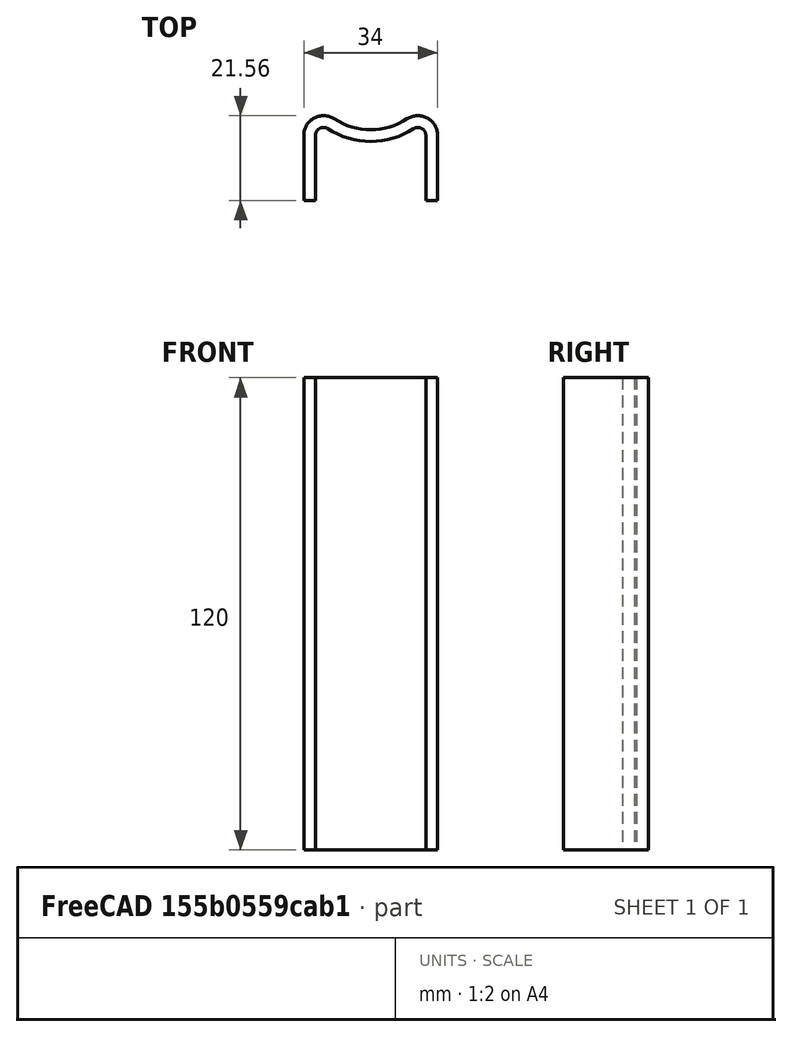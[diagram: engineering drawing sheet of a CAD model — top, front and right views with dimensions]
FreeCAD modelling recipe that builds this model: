
FCSTD DOCUMENT  (FreeCAD 0.18R4 (GitTag))
Label: door-rod-holder
License: All rights reserved
LicenseURL: http://en.wikipedia.org/wiki/All_rights_reserved
objects: Sketcher::SketchObject×1, PartDesign::Pad×1, PartDesign::Body×1
note: 4 computed .brp shape members not serialized (recipe doc carries the construction recipe); baked Part::Feature solids carry a one-line shape summary decoded from their .brp

FEATURE [Sketcher::SketchObject] Sketch
  MapMode = 5
  Support = -> [XY_Plane]
  sketch-geometry (12):
    g0: LineSegment StartX=0 StartY=0 StartZ=0 EndX=3 EndY=0 EndZ=0
    g1: LineSegment StartX=34 StartY=0 StartZ=0 EndX=34 EndY=16.561 EndZ=0
    g2: LineSegment StartX=0 StartY=16.561 StartZ=0 EndX=0 EndY=0 EndZ=0
    g3: LineSegment StartX=31 StartY=16.561 StartZ=0 EndX=31 EndY=0 EndZ=0
    g4: LineSegment StartX=3 StartY=0 StartZ=0 EndX=3 EndY=16.561 EndZ=0
    g5: LineSegment StartX=31 StartY=0 StartZ=0 EndX=34 EndY=0 EndZ=0
    g6: ArcOfCircle CenterX=5 CenterY=16.561 CenterZ=0 NormalX=0 NormalY=0 NormalZ=1 AngleXU=0 Radius=5 StartAngle=0.993864 EndAngle=3.14159
    g7: ArcOfCircle CenterX=17 CenterY=35.0001 CenterZ=0 NormalX=0 NormalY=0 NormalZ=1 AngleXU=0 Radius=17 StartAngle=4.13546 EndAngle=5.28932
    g8: ArcOfCircle CenterX=29 CenterY=16.561 CenterZ=0 NormalX=0 NormalY=0 NormalZ=1 AngleXU=0 Radius=5 StartAngle=6.28319 EndAngle=8.43092
    g9: ArcOfCircle CenterX=29 CenterY=16.561 CenterZ=0 NormalX=0 NormalY=0 NormalZ=1 AngleXU=0 Radius=2 StartAngle=3.71277e-08 EndAngle=2.14773
    g10: ArcOfCircle CenterX=17 CenterY=35.0001 CenterZ=0 NormalX=0 NormalY=0 NormalZ=1 AngleXU=0 Radius=20 StartAngle=4.13546 EndAngle=5.28932
    g11: ArcOfCircle CenterX=5 CenterY=16.561 CenterZ=0 NormalX=0 NormalY=0 NormalZ=1 AngleXU=0 Radius=2 StartAngle=0.993865 EndAngle=3.14159
  constraints (40):
    c: Coincident(g5,g1)
    c: Coincident(g2,g0)
    c: Horizontal(g0)
    c: Vertical(g1)
    c: Vertical(g2)
    c: Coincident(g0,g-1)
    c: Vertical(g3)
    c: Vertical(g4)
    c: Tangent(g0,g5)
    c: Coincident(g4,g0)
    c: Coincident(g3,g5)
    c: Coincident(g6,g2)
    c: Coincident(g7,g6)
    c: Coincident(g8,g7)
    c: Coincident(g8,g1)
    c: Coincident(g9,g3)
    c: Coincident(g10,g9)
    c: Coincident(g11,g10)
    c: Coincident(g11,g4)
    c: DistanceX(g3,g1) = 3
    c: DistanceX(g0,g0) = 3
    c: DistanceX(g0,g1) = 34
    c: Radius(g8) = 5
    c: Radius(g9) = 2
    c: Radius(g6) = 5
    c: Radius(g11) = 2
    c: Radius(g7) = 17
    c: Radius(g10) = 20
    c: Tangent(g6,g7)
    c: Tangent(g6,g2)
    c: DistanceY(g2,g2) = 16.561
    c: Tangent(g4,g11)
    c: Tangent(g10,g11)
    c: Equal(g4,g2)
    c: Tangent(g3,g9)
    c: Tangent(g10,g9)
    c: Equal(g3,g4)
    c: Equal(g1,g4)
    c: Tangent(g8,g1)
    c: Tangent(g8,g7)
FEATURE [PartDesign::Pad] Pad
  Length = 120
  Length2 = 100
  Profile = -> Sketch
  Refine = true
  Type = 0
FEATURE [PartDesign::Body] Body
  Group = -> [Sketch,Pad]
  Origin = -> Origin
  Tip = -> Pad
